# Revit family: FJ4.203PR
name_source: partatom
category: Plumbing Fixtures
revit_build: Autodesk Revit Architecture 2012 (Build: 20110309_2315(x64)
units: mm (PartAtom-declared; Revit-internal decimal feet)

## types (1)
- FJ4.203PR
    Assembly Code = D2010
    CW Connection = Yes
    CWFU = 0
    Concealed push button assembly = C-KM9.15
    Cost = 0 $
    Default Elevation = 0' - 0"
    Description = Concealed type. Back entry + vandal resistant guide tube pushbutton assembly
    Flushvalve top cover = C-FJC1.2
    HW Connection = No
    HWFU = 0
    Keynote = 3/4" "Ball-o-Stop" control inlet. Water can be shut off at the VALVE for servicing
    Manufacturer = COBRA
    Material = DZR - Brass
    Model = FJ4.203PR
    Piston assembly C-FJ8.10 = C-FJ8.10
    Pushbutton assembly = C-FJ8.20
    Range = Junior Flushmaster Flushvalves
    Rubber pan connector = C-FJV1.7
    Top cover = C-FJC1.2
    Type Comments = SANS 1240
    URL = http://www.cobra.co.za
    Vent Connection = No
    WFU = 0
    Waste Connection = No

## geometry (parser evidence)
native form markers: Blend x5
no freeform markers — native parametric forms only
